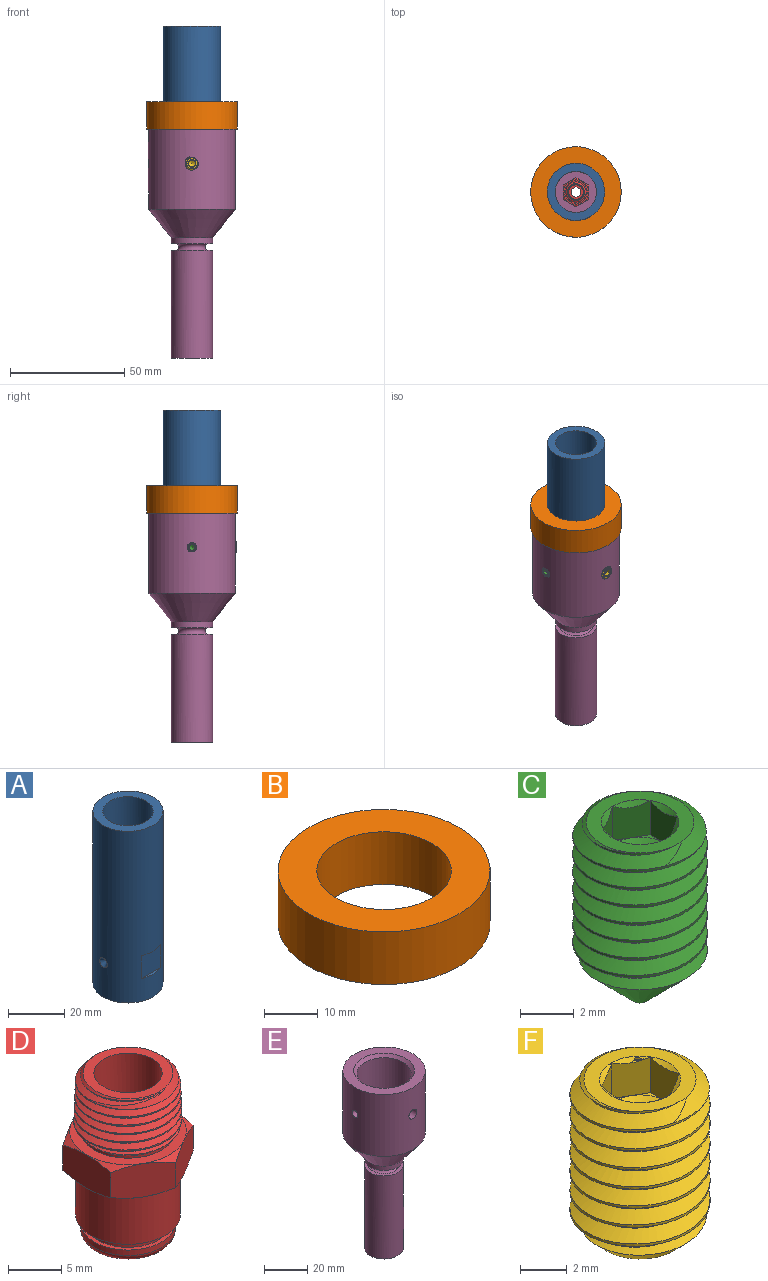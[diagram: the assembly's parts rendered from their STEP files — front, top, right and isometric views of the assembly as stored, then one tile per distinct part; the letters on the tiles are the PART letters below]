
ASSEMBLY  parts=6 mates=7
PART A: 8 faces, bbox 25x25x75 mm
  f0: cylinder r=12.5mm len=75mm, axis (0,0,-1), area 5778mm2, adj f1,f2,f3,f4,f5,f7
  f1: plane 25x25mm, normal (0,0,1), area 236.4mm2, adj f0,f6
  f2: plane 25x25mm, normal (0,0,-1), area 236.4mm2, adj f0,f6
  f3: plane 9.8x1mm, normal (0,0,1), area 6.6mm2, adj f0,f5
  f4: plane 9.8x1mm, normal (0,0,-1), area 6.6mm2, adj f0,f5
  f5: plane 10x9.8mm, normal (0,-1,0), area 98mm2, adj f0,f3,f4
  f6: cylinder r=9mm len=75mm, axis (0,0,-1), area 4241.2mm2, adj f1,f2
  f7: cone r=0mm half-angle=45deg, axis (-1,0,0), area 16.5mm2, adj f0
PART B: 4 faces, bbox 39.5x39.5x12 mm
  f0: cylinder r=12.53mm len=25.05mm, axis (0,0,-1), area 944.4mm2, adj f2,f3
  f1: cylinder r=19.75mm len=39.5mm, axis (0,0,-1), area 1489.1mm2, adj f2,f3
  f2: plane 39.5x39.5mm, normal (0,0,1), area 732.6mm2, adj f0,f1
  f3: plane 39.5x39.5mm, normal (0,0,-1), area 732.6mm2, adj f0,f1
PART C: 27 faces, bbox 5.5x5.5x8.9 mm
  f0: plane 1.08x0.63mm, normal (0,0,1), area 0.1mm2, adj f24,f25,f26
  f1: plane 1.25x0.36mm, normal (0,0,1), area 0.1mm2, adj f20,f25,f26
  f2: plane 1.08x0.63mm, normal (0,0,1), area 0.1mm2, adj f20,f21,f26
  f3: plane 1.08x0.63mm, normal (0,0,1), area 0.1mm2, adj f21,f22,f26
  f4: plane 1.25x0.36mm, normal (0,0,1), area 0.1mm2, adj f22,f23,f26
  f5: cone r=0.33mm half-angle=45deg, axis (0,0,1), area 22mm2, adj f6,f9,f10,f11,f12
  f6: cylinder r=2.5mm len=5.48mm, axis (0,0,-1), area 10.7mm2, adj f5,f7,f10,f12
  f7: cone r=2.5mm half-angle=55deg, axis (0,0,-1), area 4.1mm2, adj f6,f8,f10,f12
  f8: plane 4x3.99mm, normal (0,0,1), area 6mm2, adj f7,f10,f11,f12,f13,f14,f15,f16
  f9: plane 0.65x0.65mm, normal (0,0,-1), area 0.3mm2, adj f5
  f10: bspline ~6.8x5mm, area 62.3mm2, adj f5,f6,f7,f8,f11
  f11: cylinder r=1.98mm len=6.34mm, axis (0,0,-1), area 9.9mm2, adj f5,f8,f10,f12
  f12: bspline ~6.8x5mm, area 62.4mm2, adj f5,f6,f7,f8,f11
  f13: cone r=1.44mm half-angle=45deg, axis (0,0,1), area 0mm2, adj f8,f20
  f14: cone r=1.44mm half-angle=45deg, axis (0,0,1), area 0mm2, adj f8,f21
  f15: cone r=1.44mm half-angle=45deg, axis (0,0,1), area 0mm2, adj f8,f22
  f16: cone r=1.44mm half-angle=45deg, axis (0,0,1), area 0mm2, adj f8,f23
  f17: cone r=1.44mm half-angle=45deg, axis (0,0,1), area 0mm2, adj f8,f24
  f18: cone r=1.44mm half-angle=45deg, axis (0,0,1), area 0mm2, adj f8,f25
  f19: plane 1.08x0.63mm, normal (0,0,1), area 0.1mm2, adj f23,f24,f26
  f20: plane 2.11x1.8mm, normal (0.5,-0.87,0), area 2.1mm2, adj f1,f2,f13,f21,f25
  f21: plane 2.11x1.99mm, normal (1,0,0), area 2.1mm2, adj f2,f3,f14,f20,f22
  f22: plane 2.11x1.8mm, normal (0.5,0.87,0), area 2.1mm2, adj f3,f4,f15,f21,f23
  f23: plane 2.11x1.8mm, normal (-0.5,0.87,0), area 2.1mm2, adj f4,f16,f19,f22,f24
  f24: plane 2.11x1.99mm, normal (-1,0,0), area 2.1mm2, adj f0,f17,f19,f23,f25
  f25: plane 2.11x1.8mm, normal (-0.5,-0.87,0), area 2.1mm2, adj f0,f1,f18,f20,f24
  f26: cone r=1.25mm half-angle=60deg, axis (0,0,1), area 5.7mm2, adj f0,f1,f2,f3,f4,f19
PART D: 46 faces, bbox 13.2x13.2x19.6 mm
  f0: plane 2.03x2.03mm, normal (0.5,-0.87,0), area 4.8mm2, adj f1,f5,f43,f44
  f1: plane 2.35x2.03mm, normal (1,0,0), area 4.8mm2, adj f0,f2,f43,f44
  f2: plane 2.03x2.03mm, normal (0.5,0.87,0), area 4.8mm2, adj f1,f3,f43,f44
  f3: plane 2.03x2.03mm, normal (-0.5,0.87,0), area 4.8mm2, adj f2,f4,f43,f44
  f4: plane 2.35x2.03mm, normal (-1,0,0), area 4.8mm2, adj f3,f5,f43,f44
  f5: plane 2.03x2.03mm, normal (-0.5,-0.87,0), area 4.8mm2, adj f0,f4,f43,f44
  f6: plane 11x11mm, normal (0,0,-1), area 18.1mm2, adj f22,f23,f24,f25,f26,f27,f34
  f7: plane 11x11mm, normal (0,0,1), area 33.2mm2, adj f13,f16,f17,f18,f19,f20,f21
  f8: cone r=4.93mm half-angle=1.8deg, axis (0,0,-1), area 18.6mm2, adj f10,f11,f12,f14
  f9: bspline ~9.41x9.34mm, area 21.7mm2, adj f10,f11,f12,f14
  f10: bspline ~10.78x10.72mm, area 120.8mm2, adj f8,f9,f12,f14
  f11: bspline ~10.84x10.78mm, area 126.1mm2, adj f8,f9,f12,f14
  f12: cone r=5.24mm half-angle=45deg, axis (0,0,1), area 16.3mm2, adj f8,f9,f10,f11,f13
  f13: cylinder r=4.43mm len=8.87mm, axis (0,0,1), area 7.9mm2, adj f7,f12
  f14: cone r=4.23mm half-angle=45deg, axis (0,0,-1), area 16.6mm2, adj f8,f9,f10,f11,f15
  f15: plane 8.47x8.47mm, normal (0,0,1), area 23.8mm2, adj f14,f45
  f16: cone r=5.5mm half-angle=60deg, axis (0,0,-1), area 3mm2, adj f7,f28,f29
  f17: cone r=5.5mm half-angle=60deg, axis (0,0,-1), area 3mm2, adj f7,f29,f30
  f18: cone r=5.5mm half-angle=60deg, axis (0,0,-1), area 3mm2, adj f7,f30,f31
  f19: cone r=5.5mm half-angle=60deg, axis (0,0,-1), area 3mm2, adj f7,f31,f32
  f20: cone r=5.5mm half-angle=60deg, axis (0,0,-1), area 3mm2, adj f7,f32,f33
  f21: cone r=5.5mm half-angle=60deg, axis (0,0,-1), area 3mm2, adj f7,f28,f33
  f22: cone r=5.5mm half-angle=60deg, axis (0,0,1), area 3mm2, adj f6,f32,f33
  f23: cone r=5.5mm half-angle=60deg, axis (0,0,1), area 3mm2, adj f6,f31,f32
  f24: cone r=5.5mm half-angle=60deg, axis (0,0,1), area 3mm2, adj f6,f30,f31
  f25: cone r=5.5mm half-angle=60deg, axis (0,0,1), area 3mm2, adj f6,f29,f30
  f26: cone r=5.5mm half-angle=60deg, axis (0,0,1), area 3mm2, adj f6,f28,f29
  f27: cone r=5.5mm half-angle=60deg, axis (0,0,1), area 3mm2, adj f6,f28,f33
  f28: plane 6.88x4.38mm, normal (-1,0,0), area 22.3mm2, adj f16,f21,f26,f27,f29,f33
  f29: plane 6.02x4.38mm, normal (-0.5,-0.87,0), area 22.3mm2, adj f16,f17,f25,f26,f28,f30
  f30: plane 6.02x4.38mm, normal (0.5,-0.87,0), area 22.3mm2, adj f17,f18,f24,f25,f29,f31
  f31: plane 6.88x4.38mm, normal (1,0,0), area 22.3mm2, adj f18,f19,f23,f24,f30,f32
  f32: plane 6.02x4.38mm, normal (0.5,0.87,0), area 22.3mm2, adj f19,f20,f22,f23,f31,f33
  f33: plane 6.02x4.38mm, normal (-0.5,0.87,0), area 22.3mm2, adj f20,f21,f22,f27,f28,f32
  f34: cylinder r=4.95mm len=9.9mm, axis (0,0,1), area 178.1mm2, adj f6,f35
  f35: plane 9.9x9.9mm, normal (0,0,-1), area 26.5mm2, adj f34,f36
  f36: cylinder r=4.01mm len=8.02mm, axis (0,0,1), area 25.6mm2, adj f35,f37
  f37: plane 8.91x8.91mm, normal (0,0,1), area 11.8mm2, adj f36,f38
  f38: cylinder r=4.46mm len=8.91mm, axis (0,0,1), area 17.8mm2, adj f37,f39
  f39: torus R=3.69mm, axis (0,0,1), area 31.4mm2, adj f38,f40
  f40: plane 7.39x7.39mm, normal (0,0,-1), area 3.1mm2, adj f39,f41
  f41: cone r=3.17mm half-angle=45deg, axis (0,0,-1), area 11.4mm2, adj f40,f42
  f42: cylinder r=3.17mm len=11.61mm, axis (0,0,1), area 231.6mm2, adj f41,f43
  f43: plane 6.35x6.35mm, normal (0,0,-1), area 17.4mm2, adj f0,f1,f2,f3,f4,f5,f42
  f44: plane 6.44x6.44mm, normal (0,0,1), area 18.2mm2, adj f0,f1,f2,f3,f4,f5,f45
  f45: cylinder r=3.22mm len=6.44mm, axis (0,0,1), area 94.5mm2, adj f15,f44
PART E: 17 faces, bbox 38x38x100 mm
  f0: cylinder r=9mm len=18mm, axis (0,0,1), area 141.4mm2, adj f7,f15
  f1: cylinder r=4mm len=40mm, axis (0,0,1), area 1005.3mm2, adj f4,f13
  f2: cylinder r=19mm len=38mm, axis (0,0,1), area 4146.6mm2, adj f7,f8,f9,f10
  f3: cylinder r=12.5mm len=33.5mm, axis (0,0,1), area 2599.1mm2, adj f4,f9,f10,f11
  f4: plane 25x25mm, normal (0,0,1), area 440.6mm2, adj f1,f3
  f5: plane 18x18mm, normal (0,0,-1), area 234.8mm2, adj f6,f12
  f6: cylinder r=9mm len=47mm, axis (0,0,1), area 2657.8mm2, adj f5,f14
  f7: cone r=19mm half-angle=38.7deg, axis (0,0,1), area 1408.1mm2, adj f0,f2
  f8: plane 38x38mm, normal (0,0,1), area 518.4mm2, adj f2,f11
  f9: cylinder r=2.55mm len=6.76mm, axis (0,-1,0), area 105mm2, adj f2,f3
  f10: cylinder r=1.9mm len=6.65mm, axis (-1,0,0), area 77.8mm2, adj f2,f3
  f11: cone r=12.5mm half-angle=45deg, axis (0,0,1), area 176.6mm2, adj f3,f8
  f12: cylinder r=2.5mm len=25mm, axis (0,0,-1), area 392.7mm2, adj f5,f13
  f13: plane 8x8mm, normal (0,0,1), area 30.6mm2, adj f1,f12
  f14: plane 18x18mm, normal (0,0,1), area 89.3mm2, adj f6,f16
  f15: plane 18x18mm, normal (0,0,-1), area 89.3mm2, adj f0,f16
  f16: torus R=7.25mm, axis (0,0,-1), area 186.4mm2, adj f14,f15
PART F: 28 faces, bbox 6.6x6.6x9.2 mm
  f0: plane 1.3x0.75mm, normal (0,0,1), area 0.1mm2, adj f21,f22,f27
  f1: plane 1.5x0.43mm, normal (0,0,1), area 0.1mm2, adj f21,f26,f27
  f2: plane 1.3x0.75mm, normal (0,0,1), area 0.1mm2, adj f25,f26,f27
  f3: plane 1.3x0.75mm, normal (0,0,1), area 0.1mm2, adj f24,f25,f27
  f4: plane 1.5x0.43mm, normal (0,0,1), area 0.1mm2, adj f23,f24,f27
  f5: plane 4.81x4.77mm, normal (0,0,1), area 8.6mm2, adj f6,f11,f12,f13,f14,f15,f16,f17
  f6: cone r=3mm half-angle=55deg, axis (0,0,-1), area 5.7mm2, adj f5,f7,f11,f13
  f7: cylinder r=3mm len=6.58mm, axis (0,0,-1), area 15.5mm2, adj f6,f9,f11,f13
  f8: cone r=2mm half-angle=45deg, axis (0,0,1), area 12.2mm2, adj f9,f10,f11,f12
  f9: cone r=2mm half-angle=45deg, axis (0,0,1), area 2mm2, adj f7,f8,f11,f13
  f10: plane 4x4mm, normal (0,0,-1), area 12.6mm2, adj f8
  f11: bspline ~8.25x6mm, area 89.7mm2, adj f5,f6,f7,f8,f9,f12
  f12: cylinder r=2.35mm len=7.65mm, axis (0,0,1), area 14.1mm2, adj f5,f8,f11,f13
  f13: bspline ~8.25x6mm, area 89.8mm2, adj f5,f6,f7,f9,f12
  f14: cone r=1.73mm half-angle=55deg, axis (0,0,1), area 0mm2, adj f5,f21
  f15: cone r=1.73mm half-angle=55deg, axis (0,0,1), area 0mm2, adj f5,f22
  f16: cone r=1.73mm half-angle=55deg, axis (0,0,1), area 0mm2, adj f5,f23
  f17: cone r=1.73mm half-angle=55deg, axis (0,0,1), area 0mm2, adj f5,f24
  f18: cone r=1.73mm half-angle=55deg, axis (0,0,1), area 0mm2, adj f5,f25
  f19: cone r=1.73mm half-angle=55deg, axis (0,0,1), area 0mm2, adj f5,f26
  f20: plane 1.3x0.75mm, normal (0,0,1), area 0.1mm2, adj f22,f23,f27
  f21: plane 2.44x2.07mm, normal (0.5,-0.87,0), area 3.1mm2, adj f0,f1,f14,f22,f26
  f22: plane 2.44x2.3mm, normal (1,0,0), area 3.1mm2, adj f0,f15,f20,f21,f23
  f23: plane 2.44x2.07mm, normal (0.5,0.87,0), area 3.1mm2, adj f4,f16,f20,f22,f24
  f24: plane 2.44x2.07mm, normal (-0.5,0.87,0), area 3.1mm2, adj f3,f4,f17,f23,f25
  f25: plane 2.44x2.3mm, normal (-1,0,0), area 3.1mm2, adj f2,f3,f18,f24,f26
  f26: plane 2.44x2.07mm, normal (-0.5,-0.87,0), area 3.1mm2, adj f1,f2,f19,f21,f25
  f27: cone r=1.5mm half-angle=60deg, axis (0,0,1), area 8.2mm2, adj f0,f1,f2,f3,f4,f20
PLACE A at identity
PLACE B at identity
PLACE C rot(axis=(0.29,-0.91,-0.29),95.1deg) t=(-14.92,0,15)mm
PLACE D rot(axis=(1,0,0),180deg) t=(0,0,-11.7)mm
PLACE E at identity
PLACE F rot(axis=(0.78,0.44,-0.44),104.3deg) t=(0,-15.5,15)mm
MATE slider B.f0 <-> A.f0  axis (0,0,-1) through (0,0,42)mm
MATE fastened E.f0 <-> B.f1  axis (0,0,1) through (0,0,30)mm
MATE fastened D.f8 <-> E.f0  axis (0,0,-1) through (0,0,-5)mm
MATE planar A.f5 <-> F.f6  axis (0,-1,0) through (0,-11.5,15)mm
MATE planar A.f0 <-> B.f1  axis (0,0,-1) through (0,0,0)mm
MATE cylindrical F.f6 <-> E.f9  axis (0,1,0) through (0,-11.5,15)mm
MATE cylindrical C.f5 <-> E.f10  axis (-1,0,0) through (-12.01,0,15)mm
